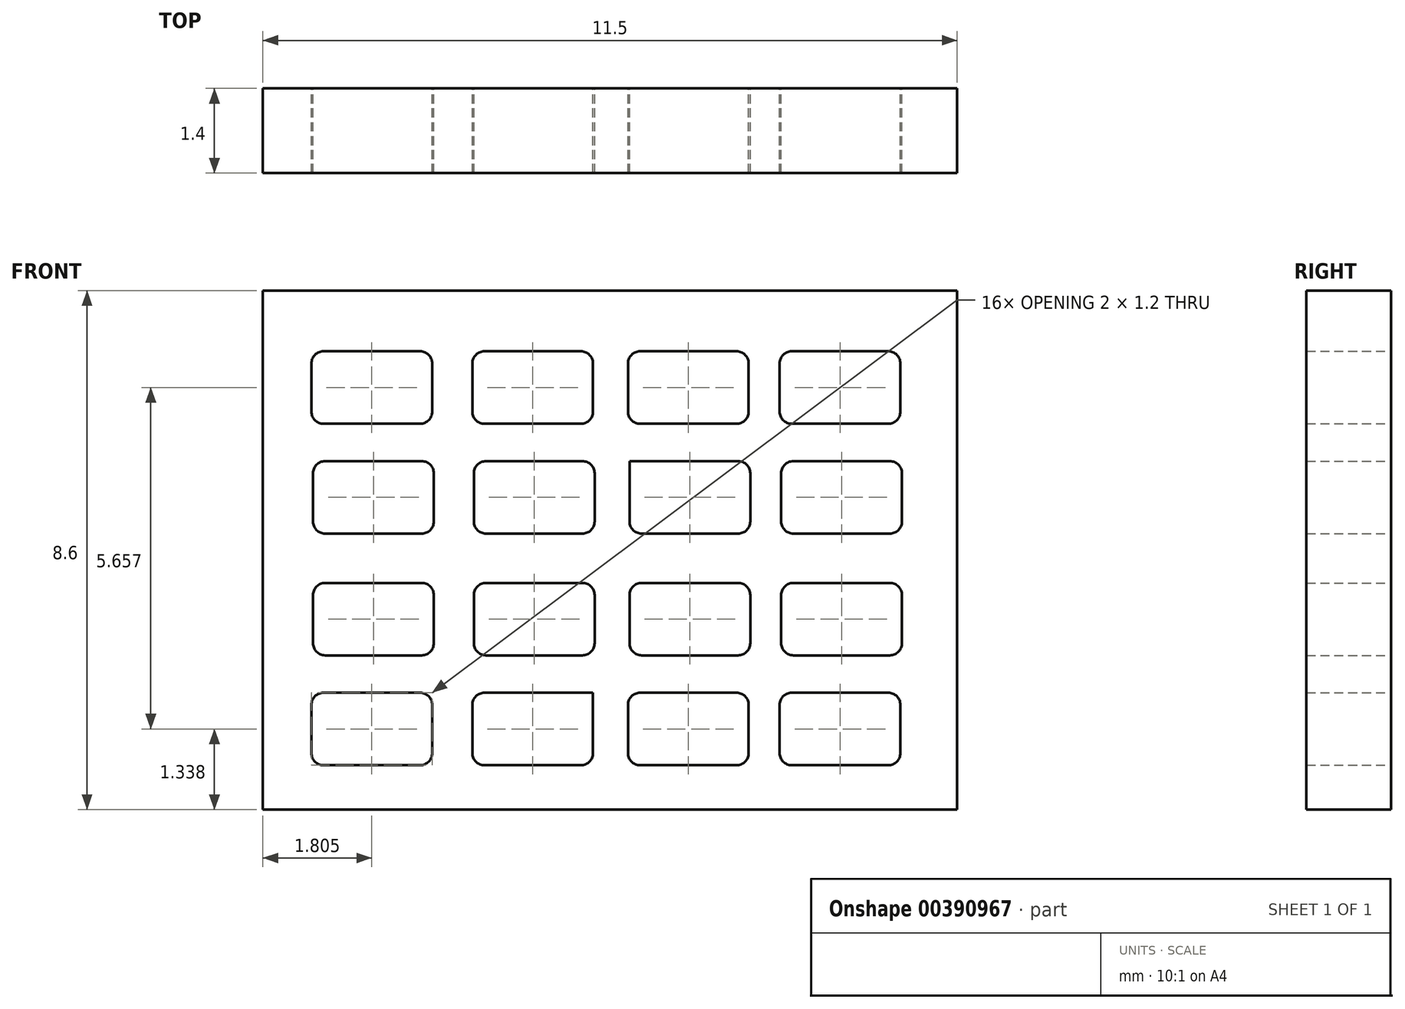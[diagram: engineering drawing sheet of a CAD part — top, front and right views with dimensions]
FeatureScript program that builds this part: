
annotation { "Feature Type Name" : "Feature", "Feature Type Description" : "" }
export const myFeature = defineFeature(function(context is Context, id is Id, definition is map)
    precondition{}
    {
        {
            var Q0;
            Q0=qCreatedBy(makeId("Front.planeOp"),FACE);
            var sketch = newSketch(context, id + "F0", { "sketchPlane" : qUnion([Q0])});
            skLineSegment(sketch, "E0.bottom", {"start": v(-11.5, 8.6) * mm, "end": v(0, 8.6) * mm});
            skLineSegment(sketch, "E0.top", {"start": v(-11.5, 0) * mm, "end": v(0, 0) * mm});
            skLineSegment(sketch, "E0.left", {"start": v(-11.5, 8.6) * mm, "end": v(-11.5, 0) * mm});
            skLineSegment(sketch, "E0.right", {"start": v(0, 8.6) * mm, "end": v(0, 0) * mm});
            skSolve(sketch);
        }
        {
            var Q0;
            Q0=qCreatedBy(makeId("Front.planeOp"),FACE);
            var sketch = newSketch(context, id + "F1", { "sketchPlane" : qUnion([Q0])});
            skLineSegment(sketch, "E1.bottom", {"start": v(-10.7, 7.6) * mm, "end": v(-8.7, 7.6) * mm});
            skLineSegment(sketch, "E1.top", {"start": v(-10.7, 6.4) * mm, "end": v(-8.7, 6.4) * mm});
            skLineSegment(sketch, "E1.left", {"start": v(-10.7, 7.6) * mm, "end": v(-10.7, 6.4) * mm});
            skLineSegment(sketch, "E1.right", {"start": v(-8.7, 7.6) * mm, "end": v(-8.7, 6.4) * mm});
            skLineSegment(sketch, "E2.bottom", {"start": v(-8.03, 7.6) * mm, "end": v(-6.03, 7.6) * mm});
            skLineSegment(sketch, "E2.top", {"start": v(-8.03, 6.4) * mm, "end": v(-6.03, 6.4) * mm});
            skLineSegment(sketch, "E2.left", {"start": v(-8.03, 7.6) * mm, "end": v(-8.03, 6.4) * mm});
            skLineSegment(sketch, "E2.right", {"start": v(-6.03, 7.6) * mm, "end": v(-6.03, 6.4) * mm});
            skLineSegment(sketch, "E3.bottom", {"start": v(-5.45, 7.6) * mm, "end": v(-3.45, 7.6) * mm});
            skLineSegment(sketch, "E3.top", {"start": v(-5.45, 6.4) * mm, "end": v(-3.45, 6.4) * mm});
            skLineSegment(sketch, "E3.left", {"start": v(-5.45, 7.6) * mm, "end": v(-5.45, 6.4) * mm});
            skLineSegment(sketch, "E3.right", {"start": v(-3.45, 7.6) * mm, "end": v(-3.45, 6.4) * mm});
            skLineSegment(sketch, "E4.bottom", {"start": v(-2.94, 7.6) * mm, "end": v(-0.94, 7.6) * mm});
            skLineSegment(sketch, "E4.top", {"start": v(-2.94, 6.4) * mm, "end": v(-0.94, 6.4) * mm});
            skLineSegment(sketch, "E4.left", {"start": v(-2.94, 7.6) * mm, "end": v(-2.94, 6.4) * mm});
            skLineSegment(sketch, "E4.right", {"start": v(-0.94, 7.6) * mm, "end": v(-0.94, 6.4) * mm});
            skLineSegment(sketch, "E5.MirrorCS", {"start": v(-10.67, 5.77) * mm, "end": v(-8.67, 5.77) * mm});
            skLineSegment(sketch, "E6.MirrorCS", {"start": v(-8.67, 4.57) * mm, "end": v(-8.67, 5.77) * mm});
            skLineSegment(sketch, "E7.MirrorCS", {"start": v(-10.67, 4.57) * mm, "end": v(-8.67, 4.57) * mm});
            skLineSegment(sketch, "E8.MirrorCS", {"start": v(-10.67, 4.57) * mm, "end": v(-10.67, 5.77) * mm});
            skLineSegment(sketch, "E9.MirrorCS", {"start": v(-8, 4.57) * mm, "end": v(-8, 5.77) * mm});
            skLineSegment(sketch, "E10.MirrorCS", {"start": v(-8, 4.57) * mm, "end": v(-6, 4.57) * mm});
            skLineSegment(sketch, "E11.MirrorCS", {"start": v(-8, 5.77) * mm, "end": v(-6, 5.77) * mm});
            skLineSegment(sketch, "E12.MirrorCS", {"start": v(-6, 4.57) * mm, "end": v(-6, 5.77) * mm});
            skLineSegment(sketch, "E13.MirrorCS", {"start": v(-5.43, 4.57) * mm, "end": v(-5.43, 5.77) * mm});
            skLineSegment(sketch, "E14.MirrorCS", {"start": v(-5.43, 5.77) * mm, "end": v(-3.43, 5.77) * mm});
            skLineSegment(sketch, "E15.MirrorCS", {"start": v(-3.43, 4.57) * mm, "end": v(-3.43, 5.77) * mm});
            skLineSegment(sketch, "E16.MirrorCS", {"start": v(-5.43, 4.57) * mm, "end": v(-3.43, 4.57) * mm});
            skLineSegment(sketch, "E17.MirrorCS", {"start": v(-2.91, 4.57) * mm, "end": v(-0.91, 4.57) * mm});
            skLineSegment(sketch, "E18.MirrorCS", {"start": v(-2.91, 4.57) * mm, "end": v(-2.91, 5.77) * mm});
            skLineSegment(sketch, "E19.MirrorCS", {"start": v(-2.91, 5.77) * mm, "end": v(-0.91, 5.77) * mm});
            skLineSegment(sketch, "E20.MirrorCS", {"start": v(-0.91, 4.57) * mm, "end": v(-0.91, 5.77) * mm});
            skLineSegment(sketch, "E21.MirrorCS", {"start": v(-10.67, 3.76) * mm, "end": v(-10.67, 2.56) * mm});
            skLineSegment(sketch, "E22.MirrorCS", {"start": v(-5.43, 3.76) * mm, "end": v(-3.43, 3.76) * mm});
            skLineSegment(sketch, "E23.MirrorCS", {"start": v(-6, 3.76) * mm, "end": v(-6, 2.56) * mm});
            skLineSegment(sketch, "E24.MirrorCS", {"start": v(-2.94, 0.74) * mm, "end": v(-0.94, 0.74) * mm});
            skLineSegment(sketch, "E25.MirrorCS", {"start": v(-8.67, 3.76) * mm, "end": v(-8.67, 2.56) * mm});
            skLineSegment(sketch, "E26.MirrorCS", {"start": v(-2.91, 3.76) * mm, "end": v(-2.91, 2.56) * mm});
            skLineSegment(sketch, "E27.MirrorCS", {"start": v(-3.45, 0.74) * mm, "end": v(-3.45, 1.94) * mm});
            skLineSegment(sketch, "E28.MirrorCS", {"start": v(-3.43, 3.76) * mm, "end": v(-3.43, 2.56) * mm});
            skLineSegment(sketch, "E29.MirrorCS", {"start": v(-8, 3.76) * mm, "end": v(-8, 2.56) * mm});
            skLineSegment(sketch, "E30.MirrorCS", {"start": v(-5.45, 0.74) * mm, "end": v(-5.45, 1.94) * mm});
            skLineSegment(sketch, "E31.MirrorCS", {"start": v(-10.67, 2.56) * mm, "end": v(-8.67, 2.56) * mm});
            skLineSegment(sketch, "E32.MirrorCS", {"start": v(-5.45, 0.74) * mm, "end": v(-3.45, 0.74) * mm});
            skLineSegment(sketch, "E33.MirrorCS", {"start": v(-5.45, 1.94) * mm, "end": v(-3.45, 1.94) * mm});
            skLineSegment(sketch, "E34.MirrorCS", {"start": v(-0.91, 3.76) * mm, "end": v(-0.91, 2.56) * mm});
            skLineSegment(sketch, "E35.MirrorCS", {"start": v(-5.43, 2.56) * mm, "end": v(-3.43, 2.56) * mm});
            skLineSegment(sketch, "E36.MirrorCS", {"start": v(-8, 2.56) * mm, "end": v(-6, 2.56) * mm});
            skLineSegment(sketch, "E37.MirrorCS", {"start": v(-10.67, 3.76) * mm, "end": v(-8.67, 3.76) * mm});
            skLineSegment(sketch, "E38.MirrorCS", {"start": v(-8, 3.76) * mm, "end": v(-6, 3.76) * mm});
            skLineSegment(sketch, "E39.MirrorCS", {"start": v(-2.91, 2.56) * mm, "end": v(-0.91, 2.56) * mm});
            skLineSegment(sketch, "E40.MirrorCS", {"start": v(-6.03, 0.74) * mm, "end": v(-6.03, 1.94) * mm});
            skLineSegment(sketch, "E41.MirrorCS", {"start": v(-8.03, 0.74) * mm, "end": v(-8.03, 1.94) * mm});
            skLineSegment(sketch, "E42.MirrorCS", {"start": v(-8.03, 1.94) * mm, "end": v(-6.03, 1.94) * mm});
            skLineSegment(sketch, "E43.MirrorCS", {"start": v(-2.94, 1.94) * mm, "end": v(-0.94, 1.94) * mm});
            skLineSegment(sketch, "E44.MirrorCS", {"start": v(-2.94, 0.74) * mm, "end": v(-2.94, 1.94) * mm});
            skLineSegment(sketch, "E45.MirrorCS", {"start": v(-0.94, 0.74) * mm, "end": v(-0.94, 1.94) * mm});
            skLineSegment(sketch, "E46.MirrorCS", {"start": v(-10.7, 0.74) * mm, "end": v(-8.7, 0.74) * mm});
            skLineSegment(sketch, "E47.MirrorCS", {"start": v(-10.7, 1.94) * mm, "end": v(-8.7, 1.94) * mm});
            skLineSegment(sketch, "E48.MirrorCS", {"start": v(-8.03, 0.74) * mm, "end": v(-6.03, 0.74) * mm});
            skLineSegment(sketch, "E49.MirrorCS", {"start": v(-2.91, 3.76) * mm, "end": v(-0.91, 3.76) * mm});
            skLineSegment(sketch, "E50.MirrorCS", {"start": v(-5.43, 3.76) * mm, "end": v(-5.43, 2.56) * mm});
            skLineSegment(sketch, "E51.MirrorCS", {"start": v(-10.7, 0.74) * mm, "end": v(-10.7, 1.94) * mm});
            skLineSegment(sketch, "E52.MirrorCS", {"start": v(-8.7, 0.74) * mm, "end": v(-8.7, 1.94) * mm});
            skSolve(sketch);
        }
        {
            var Q0;
            Q0 = qSketchRegion(id + "F0", true);
            extrude(context, id + "F2", {"entities" : qUnion([Q0]), "depth" : 1.4 * mm});
        }
        {
            var Q0;
            Q0 = qSketchRegion(id + "F1", true);
            extrude(context, id + "F3", {"entities" : qUnion([Q0]), "operationType" : NewBodyOperationType.REMOVE, "depth" : 1.4 * mm});
        }
        {
            var Q0;
            Q0=makeQuery(id+"F3.boolean.opBoolean","COPY",EDGE,{"derivedFrom":makeQuery(id+"F3.opExtrude","SWEPT_EDGE",EDGE,{"disambiguationData":[OSD([sQuery(id+"F1.wireOp",EDGE,"E21.MirrorCS"),sQuery(id+"F1.wireOp",EDGE,"E37.MirrorCS")])]})});
            var Q1;
            Q1=makeQuery(id+"F3.boolean.opBoolean","COPY",EDGE,{"derivedFrom":makeQuery(id+"F3.opExtrude","SWEPT_EDGE",EDGE,{"disambiguationData":[OSD([sQuery(id+"F1.wireOp",EDGE,"E5.MirrorCS"),sQuery(id+"F1.wireOp",EDGE,"E8.MirrorCS")])]})});
            var Q2;
            Q2=makeQuery(id+"F3.boolean.opBoolean","COPY",EDGE,{"derivedFrom":makeQuery(id+"F3.opExtrude","SWEPT_EDGE",EDGE,{"disambiguationData":[OSD([sQuery(id+"F1.wireOp",EDGE,"E1.bottom"),sQuery(id+"F1.wireOp",EDGE,"E1.left")])]})});
            var Q3;
            Q3=makeQuery(id+"F3.boolean.opBoolean","COPY",EDGE,{"derivedFrom":makeQuery(id+"F3.opExtrude","SWEPT_EDGE",EDGE,{"disambiguationData":[OSD([sQuery(id+"F1.wireOp",EDGE,"E41.MirrorCS"),sQuery(id+"F1.wireOp",EDGE,"E42.MirrorCS")])]})});
            var Q4;
            Q4=makeQuery(id+"F3.boolean.opBoolean","COPY",EDGE,{"derivedFrom":makeQuery(id+"F3.opExtrude","SWEPT_EDGE",EDGE,{"disambiguationData":[OSD([sQuery(id+"F1.wireOp",EDGE,"E51.MirrorCS"),sQuery(id+"F1.wireOp",EDGE,"E47.MirrorCS")])]})});
            var Q5;
            Q5=makeQuery(id+"F3.boolean.opBoolean","COPY",EDGE,{"derivedFrom":makeQuery(id+"F3.opExtrude","SWEPT_EDGE",EDGE,{"disambiguationData":[OSD([sQuery(id+"F1.wireOp",EDGE,"E29.MirrorCS"),sQuery(id+"F1.wireOp",EDGE,"E38.MirrorCS")])]})});
            var Q6;
            Q6=makeQuery(id+"F3.boolean.opBoolean","COPY",EDGE,{"derivedFrom":makeQuery(id+"F3.opExtrude","SWEPT_EDGE",EDGE,{"disambiguationData":[OSD([sQuery(id+"F1.wireOp",EDGE,"E9.MirrorCS"),sQuery(id+"F1.wireOp",EDGE,"E11.MirrorCS")])]})});
            var Q7;
            Q7=makeQuery(id+"F3.boolean.opBoolean","COPY",EDGE,{"derivedFrom":makeQuery(id+"F3.opExtrude","SWEPT_EDGE",EDGE,{"disambiguationData":[OSD([sQuery(id+"F1.wireOp",EDGE,"E2.bottom"),sQuery(id+"F1.wireOp",EDGE,"E2.left")])]})});
            var Q8;
            Q8=makeQuery(id+"F3.boolean.opBoolean","COPY",EDGE,{"derivedFrom":makeQuery(id+"F3.opExtrude","SWEPT_EDGE",EDGE,{"disambiguationData":[OSD([sQuery(id+"F1.wireOp",EDGE,"E3.bottom"),sQuery(id+"F1.wireOp",EDGE,"E3.left")])]})});
            var Q9;
            Q9=makeQuery(id+"F3.boolean.opBoolean","COPY",EDGE,{"derivedFrom":makeQuery(id+"F3.opExtrude","SWEPT_EDGE",EDGE,{"disambiguationData":[OSD([sQuery(id+"F1.wireOp",EDGE,"E50.MirrorCS"),sQuery(id+"F1.wireOp",EDGE,"E22.MirrorCS")])]})});
            var Q10;
            Q10=makeQuery(id+"F3.boolean.opBoolean","COPY",EDGE,{"derivedFrom":makeQuery(id+"F3.opExtrude","SWEPT_EDGE",EDGE,{"disambiguationData":[OSD([sQuery(id+"F1.wireOp",EDGE,"E30.MirrorCS"),sQuery(id+"F1.wireOp",EDGE,"E33.MirrorCS")])]})});
            var Q11;
            Q11=makeQuery(id+"F3.boolean.opBoolean","COPY",EDGE,{"derivedFrom":makeQuery(id+"F3.opExtrude","SWEPT_EDGE",EDGE,{"disambiguationData":[OSD([sQuery(id+"F1.wireOp",EDGE,"E26.MirrorCS"),sQuery(id+"F1.wireOp",EDGE,"E49.MirrorCS")])]})});
            var Q12;
            Q12=makeQuery(id+"F3.boolean.opBoolean","COPY",EDGE,{"derivedFrom":makeQuery(id+"F3.opExtrude","SWEPT_EDGE",EDGE,{"disambiguationData":[OSD([sQuery(id+"F1.wireOp",EDGE,"E44.MirrorCS"),sQuery(id+"F1.wireOp",EDGE,"E43.MirrorCS")])]})});
            var Q13;
            Q13=makeQuery(id+"F3.boolean.opBoolean","COPY",EDGE,{"derivedFrom":makeQuery(id+"F3.opExtrude","SWEPT_EDGE",EDGE,{"disambiguationData":[OSD([sQuery(id+"F1.wireOp",EDGE,"E18.MirrorCS"),sQuery(id+"F1.wireOp",EDGE,"E19.MirrorCS")])]})});
            var Q14;
            Q14=makeQuery(id+"F3.boolean.opBoolean","COPY",EDGE,{"derivedFrom":makeQuery(id+"F3.opExtrude","SWEPT_EDGE",EDGE,{"disambiguationData":[OSD([sQuery(id+"F1.wireOp",EDGE,"E4.bottom"),sQuery(id+"F1.wireOp",EDGE,"E4.left")])]})});
            fillet(context, id + "F4", {"entities" : qUnion([Q0, Q1, Q2, Q3, Q4, Q5, Q6, Q7, Q8, Q9, Q10, Q11, Q12, Q13, Q14]), "radius" : 0.2 * mm, "tangentPropagation" : true, "allowEdgeOverflow" : false});
        }
        {
            var Q0;
            Q0=makeQuery(id+"F3.boolean.opBoolean","COPY",EDGE,{"derivedFrom":makeQuery(id+"F3.opExtrude","SWEPT_EDGE",EDGE,{"disambiguationData":[OSD([sQuery(id+"F1.wireOp",EDGE,"E52.MirrorCS"),sQuery(id+"F1.wireOp",EDGE,"E46.MirrorCS")])]})});
            var Q1;
            Q1=makeQuery(id+"F3.boolean.opBoolean","COPY",EDGE,{"derivedFrom":makeQuery(id+"F3.opExtrude","SWEPT_EDGE",EDGE,{"disambiguationData":[OSD([sQuery(id+"F1.wireOp",EDGE,"E25.MirrorCS"),sQuery(id+"F1.wireOp",EDGE,"E31.MirrorCS")])]})});
            var Q2;
            Q2=makeQuery(id+"F3.boolean.opBoolean","COPY",EDGE,{"derivedFrom":makeQuery(id+"F3.opExtrude","SWEPT_EDGE",EDGE,{"disambiguationData":[OSD([sQuery(id+"F1.wireOp",EDGE,"E6.MirrorCS"),sQuery(id+"F1.wireOp",EDGE,"E7.MirrorCS")])]})});
            var Q3;
            Q3=makeQuery(id+"F3.boolean.opBoolean","COPY",EDGE,{"derivedFrom":makeQuery(id+"F3.opExtrude","SWEPT_EDGE",EDGE,{"disambiguationData":[OSD([sQuery(id+"F1.wireOp",EDGE,"E1.top"),sQuery(id+"F1.wireOp",EDGE,"E1.right")])]})});
            var Q4;
            Q4=makeQuery(id+"F3.boolean.opBoolean","COPY",EDGE,{"derivedFrom":makeQuery(id+"F3.opExtrude","SWEPT_EDGE",EDGE,{"disambiguationData":[OSD([sQuery(id+"F1.wireOp",EDGE,"E2.top"),sQuery(id+"F1.wireOp",EDGE,"E2.right")])]})});
            var Q5;
            Q5=makeQuery(id+"F3.boolean.opBoolean","COPY",EDGE,{"derivedFrom":makeQuery(id+"F3.opExtrude","SWEPT_EDGE",EDGE,{"disambiguationData":[OSD([sQuery(id+"F1.wireOp",EDGE,"E10.MirrorCS"),sQuery(id+"F1.wireOp",EDGE,"E12.MirrorCS")])]})});
            var Q6;
            Q6=makeQuery(id+"F3.boolean.opBoolean","COPY",EDGE,{"derivedFrom":makeQuery(id+"F3.opExtrude","SWEPT_EDGE",EDGE,{"disambiguationData":[OSD([sQuery(id+"F1.wireOp",EDGE,"E36.MirrorCS"),sQuery(id+"F1.wireOp",EDGE,"E23.MirrorCS")])]})});
            var Q7;
            Q7=makeQuery(id+"F3.boolean.opBoolean","COPY",EDGE,{"derivedFrom":makeQuery(id+"F3.opExtrude","SWEPT_EDGE",EDGE,{"disambiguationData":[OSD([sQuery(id+"F1.wireOp",EDGE,"E40.MirrorCS"),sQuery(id+"F1.wireOp",EDGE,"E48.MirrorCS")])]})});
            var Q8;
            Q8=makeQuery(id+"F3.boolean.opBoolean","COPY",EDGE,{"derivedFrom":makeQuery(id+"F3.opExtrude","SWEPT_EDGE",EDGE,{"disambiguationData":[OSD([sQuery(id+"F1.wireOp",EDGE,"E27.MirrorCS"),sQuery(id+"F1.wireOp",EDGE,"E32.MirrorCS")])]})});
            var Q9;
            Q9=makeQuery(id+"F3.boolean.opBoolean","COPY",EDGE,{"derivedFrom":makeQuery(id+"F3.opExtrude","SWEPT_EDGE",EDGE,{"disambiguationData":[OSD([sQuery(id+"F1.wireOp",EDGE,"E28.MirrorCS"),sQuery(id+"F1.wireOp",EDGE,"E35.MirrorCS")])]})});
            var Q10;
            Q10=makeQuery(id+"F3.boolean.opBoolean","COPY",EDGE,{"derivedFrom":makeQuery(id+"F3.opExtrude","SWEPT_EDGE",EDGE,{"disambiguationData":[OSD([sQuery(id+"F1.wireOp",EDGE,"E15.MirrorCS"),sQuery(id+"F1.wireOp",EDGE,"E16.MirrorCS")])]})});
            var Q11;
            Q11=makeQuery(id+"F3.boolean.opBoolean","COPY",EDGE,{"derivedFrom":makeQuery(id+"F3.opExtrude","SWEPT_EDGE",EDGE,{"disambiguationData":[OSD([sQuery(id+"F1.wireOp",EDGE,"E3.top"),sQuery(id+"F1.wireOp",EDGE,"E3.right")])]})});
            var Q12;
            Q12=makeQuery(id+"F3.boolean.opBoolean","COPY",EDGE,{"derivedFrom":makeQuery(id+"F3.opExtrude","SWEPT_EDGE",EDGE,{"disambiguationData":[OSD([sQuery(id+"F1.wireOp",EDGE,"E4.top"),sQuery(id+"F1.wireOp",EDGE,"E4.right")])]})});
            var Q13;
            Q13=makeQuery(id+"F3.boolean.opBoolean","COPY",EDGE,{"derivedFrom":makeQuery(id+"F3.opExtrude","SWEPT_EDGE",EDGE,{"disambiguationData":[OSD([sQuery(id+"F1.wireOp",EDGE,"E17.MirrorCS"),sQuery(id+"F1.wireOp",EDGE,"E20.MirrorCS")])]})});
            var Q14;
            Q14=makeQuery(id+"F3.boolean.opBoolean","COPY",EDGE,{"derivedFrom":makeQuery(id+"F3.opExtrude","SWEPT_EDGE",EDGE,{"disambiguationData":[OSD([sQuery(id+"F1.wireOp",EDGE,"E34.MirrorCS"),sQuery(id+"F1.wireOp",EDGE,"E39.MirrorCS")])]})});
            var Q15;
            Q15=makeQuery(id+"F3.boolean.opBoolean","COPY",EDGE,{"derivedFrom":makeQuery(id+"F3.opExtrude","SWEPT_EDGE",EDGE,{"disambiguationData":[OSD([sQuery(id+"F1.wireOp",EDGE,"E24.MirrorCS"),sQuery(id+"F1.wireOp",EDGE,"E45.MirrorCS")])]})});
            var Q16;
            Q16=makeQuery(id+"F3.boolean.opBoolean","COPY",EDGE,{"derivedFrom":makeQuery(id+"F3.opExtrude","SWEPT_EDGE",EDGE,{"disambiguationData":[OSD([sQuery(id+"F1.wireOp",EDGE,"E24.MirrorCS"),sQuery(id+"F1.wireOp",EDGE,"E44.MirrorCS")])]})});
            var Q17;
            Q17=makeQuery(id+"F3.boolean.opBoolean","COPY",EDGE,{"derivedFrom":makeQuery(id+"F3.opExtrude","SWEPT_EDGE",EDGE,{"disambiguationData":[OSD([sQuery(id+"F1.wireOp",EDGE,"E26.MirrorCS"),sQuery(id+"F1.wireOp",EDGE,"E39.MirrorCS")])]})});
            var Q18;
            Q18=makeQuery(id+"F3.boolean.opBoolean","COPY",EDGE,{"derivedFrom":makeQuery(id+"F3.opExtrude","SWEPT_EDGE",EDGE,{"disambiguationData":[OSD([sQuery(id+"F1.wireOp",EDGE,"E17.MirrorCS"),sQuery(id+"F1.wireOp",EDGE,"E18.MirrorCS")])]})});
            var Q19;
            Q19=makeQuery(id+"F3.boolean.opBoolean","COPY",EDGE,{"derivedFrom":makeQuery(id+"F3.opExtrude","SWEPT_EDGE",EDGE,{"disambiguationData":[OSD([sQuery(id+"F1.wireOp",EDGE,"E4.top"),sQuery(id+"F1.wireOp",EDGE,"E4.left")])]})});
            var Q20;
            Q20=makeQuery(id+"F3.boolean.opBoolean","COPY",EDGE,{"derivedFrom":makeQuery(id+"F3.opExtrude","SWEPT_EDGE",EDGE,{"disambiguationData":[OSD([sQuery(id+"F1.wireOp",EDGE,"E3.top"),sQuery(id+"F1.wireOp",EDGE,"E3.left")])]})});
            var Q21;
            Q21=makeQuery(id+"F3.boolean.opBoolean","COPY",EDGE,{"derivedFrom":makeQuery(id+"F3.opExtrude","SWEPT_EDGE",EDGE,{"disambiguationData":[OSD([sQuery(id+"F1.wireOp",EDGE,"E13.MirrorCS"),sQuery(id+"F1.wireOp",EDGE,"E16.MirrorCS")])]})});
            var Q22;
            Q22=makeQuery(id+"F3.boolean.opBoolean","COPY",EDGE,{"derivedFrom":makeQuery(id+"F3.opExtrude","SWEPT_EDGE",EDGE,{"disambiguationData":[OSD([sQuery(id+"F1.wireOp",EDGE,"E35.MirrorCS"),sQuery(id+"F1.wireOp",EDGE,"E50.MirrorCS")])]})});
            var Q23;
            Q23=makeQuery(id+"F3.boolean.opBoolean","COPY",EDGE,{"derivedFrom":makeQuery(id+"F3.opExtrude","SWEPT_EDGE",EDGE,{"disambiguationData":[OSD([sQuery(id+"F1.wireOp",EDGE,"E30.MirrorCS"),sQuery(id+"F1.wireOp",EDGE,"E32.MirrorCS")])]})});
            var Q24;
            Q24=makeQuery(id+"F3.boolean.opBoolean","COPY",EDGE,{"derivedFrom":makeQuery(id+"F3.opExtrude","SWEPT_EDGE",EDGE,{"disambiguationData":[OSD([sQuery(id+"F1.wireOp",EDGE,"E41.MirrorCS"),sQuery(id+"F1.wireOp",EDGE,"E48.MirrorCS")])]})});
            var Q25;
            Q25=makeQuery(id+"F3.boolean.opBoolean","COPY",EDGE,{"derivedFrom":makeQuery(id+"F3.opExtrude","SWEPT_EDGE",EDGE,{"disambiguationData":[OSD([sQuery(id+"F1.wireOp",EDGE,"E36.MirrorCS"),sQuery(id+"F1.wireOp",EDGE,"E29.MirrorCS")])]})});
            var Q26;
            Q26=makeQuery(id+"F3.boolean.opBoolean","COPY",EDGE,{"derivedFrom":makeQuery(id+"F3.opExtrude","SWEPT_EDGE",EDGE,{"disambiguationData":[OSD([sQuery(id+"F1.wireOp",EDGE,"E9.MirrorCS"),sQuery(id+"F1.wireOp",EDGE,"E10.MirrorCS")])]})});
            var Q27;
            Q27=makeQuery(id+"F3.boolean.opBoolean","COPY",EDGE,{"derivedFrom":makeQuery(id+"F3.opExtrude","SWEPT_EDGE",EDGE,{"disambiguationData":[OSD([sQuery(id+"F1.wireOp",EDGE,"E2.top"),sQuery(id+"F1.wireOp",EDGE,"E2.left")])]})});
            var Q28;
            Q28=makeQuery(id+"F3.boolean.opBoolean","COPY",EDGE,{"derivedFrom":makeQuery(id+"F3.opExtrude","SWEPT_EDGE",EDGE,{"disambiguationData":[OSD([sQuery(id+"F1.wireOp",EDGE,"E1.top"),sQuery(id+"F1.wireOp",EDGE,"E1.left")])]})});
            var Q29;
            Q29=makeQuery(id+"F3.boolean.opBoolean","COPY",EDGE,{"derivedFrom":makeQuery(id+"F3.opExtrude","SWEPT_EDGE",EDGE,{"disambiguationData":[OSD([sQuery(id+"F1.wireOp",EDGE,"E7.MirrorCS"),sQuery(id+"F1.wireOp",EDGE,"E8.MirrorCS")])]})});
            var Q30;
            Q30=makeQuery(id+"F3.boolean.opBoolean","COPY",EDGE,{"derivedFrom":makeQuery(id+"F3.opExtrude","SWEPT_EDGE",EDGE,{"disambiguationData":[OSD([sQuery(id+"F1.wireOp",EDGE,"E21.MirrorCS"),sQuery(id+"F1.wireOp",EDGE,"E31.MirrorCS")])]})});
            var Q31;
            Q31=makeQuery(id+"F3.boolean.opBoolean","COPY",EDGE,{"derivedFrom":makeQuery(id+"F3.opExtrude","SWEPT_EDGE",EDGE,{"disambiguationData":[OSD([sQuery(id+"F1.wireOp",EDGE,"E51.MirrorCS"),sQuery(id+"F1.wireOp",EDGE,"E46.MirrorCS")])]})});
            fillet(context, id + "F5", {"entities" : qUnion([Q0, Q1, Q2, Q3, Q4, Q5, Q6, Q7, Q8, Q9, Q10, Q11, Q12, Q13, Q14, Q15, Q16, Q17, Q18, Q19, Q20, Q21, Q22, Q23, Q24, Q25, Q26, Q27, Q28, Q29, Q30, Q31]), "radius" : 0.2 * mm, "tangentPropagation" : true, "allowEdgeOverflow" : false});
        }
        {
            var Q0;
            Q0=makeQuery(id+"F3.boolean.opBoolean","COPY",EDGE,{"derivedFrom":makeQuery(id+"F3.opExtrude","SWEPT_EDGE",EDGE,{"disambiguationData":[OSD([sQuery(id+"F1.wireOp",EDGE,"E1.bottom"),sQuery(id+"F1.wireOp",EDGE,"E1.right")])]})});
            var Q1;
            Q1=makeQuery(id+"F3.boolean.opBoolean","COPY",EDGE,{"derivedFrom":makeQuery(id+"F3.opExtrude","SWEPT_EDGE",EDGE,{"disambiguationData":[OSD([sQuery(id+"F1.wireOp",EDGE,"E5.MirrorCS"),sQuery(id+"F1.wireOp",EDGE,"E6.MirrorCS")])]})});
            var Q2;
            Q2=makeQuery(id+"F3.boolean.opBoolean","COPY",EDGE,{"derivedFrom":makeQuery(id+"F3.opExtrude","SWEPT_EDGE",EDGE,{"disambiguationData":[OSD([sQuery(id+"F1.wireOp",EDGE,"E37.MirrorCS"),sQuery(id+"F1.wireOp",EDGE,"E25.MirrorCS")])]})});
            var Q3;
            Q3=makeQuery(id+"F3.boolean.opBoolean","COPY",EDGE,{"derivedFrom":makeQuery(id+"F3.opExtrude","SWEPT_EDGE",EDGE,{"disambiguationData":[OSD([sQuery(id+"F1.wireOp",EDGE,"E52.MirrorCS"),sQuery(id+"F1.wireOp",EDGE,"E47.MirrorCS")])]})});
            var Q4;
            Q4=makeQuery(id+"F3.boolean.opBoolean","COPY",EDGE,{"derivedFrom":makeQuery(id+"F3.opExtrude","SWEPT_EDGE",EDGE,{"disambiguationData":[OSD([sQuery(id+"F1.wireOp",EDGE,"E23.MirrorCS"),sQuery(id+"F1.wireOp",EDGE,"E38.MirrorCS")])]})});
            var Q5;
            Q5=makeQuery(id+"F3.boolean.opBoolean","COPY",EDGE,{"derivedFrom":makeQuery(id+"F3.opExtrude","SWEPT_EDGE",EDGE,{"disambiguationData":[OSD([sQuery(id+"F1.wireOp",EDGE,"E11.MirrorCS"),sQuery(id+"F1.wireOp",EDGE,"E12.MirrorCS")])]})});
            var Q6;
            Q6=makeQuery(id+"F3.boolean.opBoolean","COPY",EDGE,{"derivedFrom":makeQuery(id+"F3.opExtrude","SWEPT_EDGE",EDGE,{"disambiguationData":[OSD([sQuery(id+"F1.wireOp",EDGE,"E2.bottom"),sQuery(id+"F1.wireOp",EDGE,"E2.right")])]})});
            var Q7;
            Q7=makeQuery(id+"F3.boolean.opBoolean","COPY",EDGE,{"derivedFrom":makeQuery(id+"F3.opExtrude","SWEPT_EDGE",EDGE,{"disambiguationData":[OSD([sQuery(id+"F1.wireOp",EDGE,"E3.bottom"),sQuery(id+"F1.wireOp",EDGE,"E3.right")])]})});
            var Q8;
            Q8=makeQuery(id+"F3.boolean.opBoolean","COPY",EDGE,{"derivedFrom":makeQuery(id+"F3.opExtrude","SWEPT_EDGE",EDGE,{"disambiguationData":[OSD([sQuery(id+"F1.wireOp",EDGE,"E14.MirrorCS"),sQuery(id+"F1.wireOp",EDGE,"E15.MirrorCS")])]})});
            var Q9;
            Q9=makeQuery(id+"F3.boolean.opBoolean","COPY",EDGE,{"derivedFrom":makeQuery(id+"F3.opExtrude","SWEPT_EDGE",EDGE,{"disambiguationData":[OSD([sQuery(id+"F1.wireOp",EDGE,"E28.MirrorCS"),sQuery(id+"F1.wireOp",EDGE,"E22.MirrorCS")])]})});
            var Q10;
            Q10=makeQuery(id+"F3.boolean.opBoolean","COPY",EDGE,{"derivedFrom":makeQuery(id+"F3.opExtrude","SWEPT_EDGE",EDGE,{"disambiguationData":[OSD([sQuery(id+"F1.wireOp",EDGE,"E27.MirrorCS"),sQuery(id+"F1.wireOp",EDGE,"E33.MirrorCS")])]})});
            var Q11;
            Q11=makeQuery(id+"F3.boolean.opBoolean","COPY",EDGE,{"derivedFrom":makeQuery(id+"F3.opExtrude","SWEPT_EDGE",EDGE,{"disambiguationData":[OSD([sQuery(id+"F1.wireOp",EDGE,"E34.MirrorCS"),sQuery(id+"F1.wireOp",EDGE,"E49.MirrorCS")])]})});
            var Q12;
            Q12=makeQuery(id+"F3.boolean.opBoolean","COPY",EDGE,{"derivedFrom":makeQuery(id+"F3.opExtrude","SWEPT_EDGE",EDGE,{"disambiguationData":[OSD([sQuery(id+"F1.wireOp",EDGE,"E45.MirrorCS"),sQuery(id+"F1.wireOp",EDGE,"E43.MirrorCS")])]})});
            var Q13;
            Q13=makeQuery(id+"F3.boolean.opBoolean","COPY",EDGE,{"derivedFrom":makeQuery(id+"F3.opExtrude","SWEPT_EDGE",EDGE,{"disambiguationData":[OSD([sQuery(id+"F1.wireOp",EDGE,"E19.MirrorCS"),sQuery(id+"F1.wireOp",EDGE,"E20.MirrorCS")])]})});
            var Q14;
            Q14=makeQuery(id+"F3.boolean.opBoolean","COPY",EDGE,{"derivedFrom":makeQuery(id+"F3.opExtrude","SWEPT_EDGE",EDGE,{"disambiguationData":[OSD([sQuery(id+"F1.wireOp",EDGE,"E4.bottom"),sQuery(id+"F1.wireOp",EDGE,"E4.right")])]})});
            fillet(context, id + "F6", {"entities" : qUnion([Q0, Q1, Q2, Q3, Q4, Q5, Q6, Q7, Q8, Q9, Q10, Q11, Q12, Q13, Q14]), "radius" : 0.2 * mm, "tangentPropagation" : true, "allowEdgeOverflow" : false});
        }
    });
